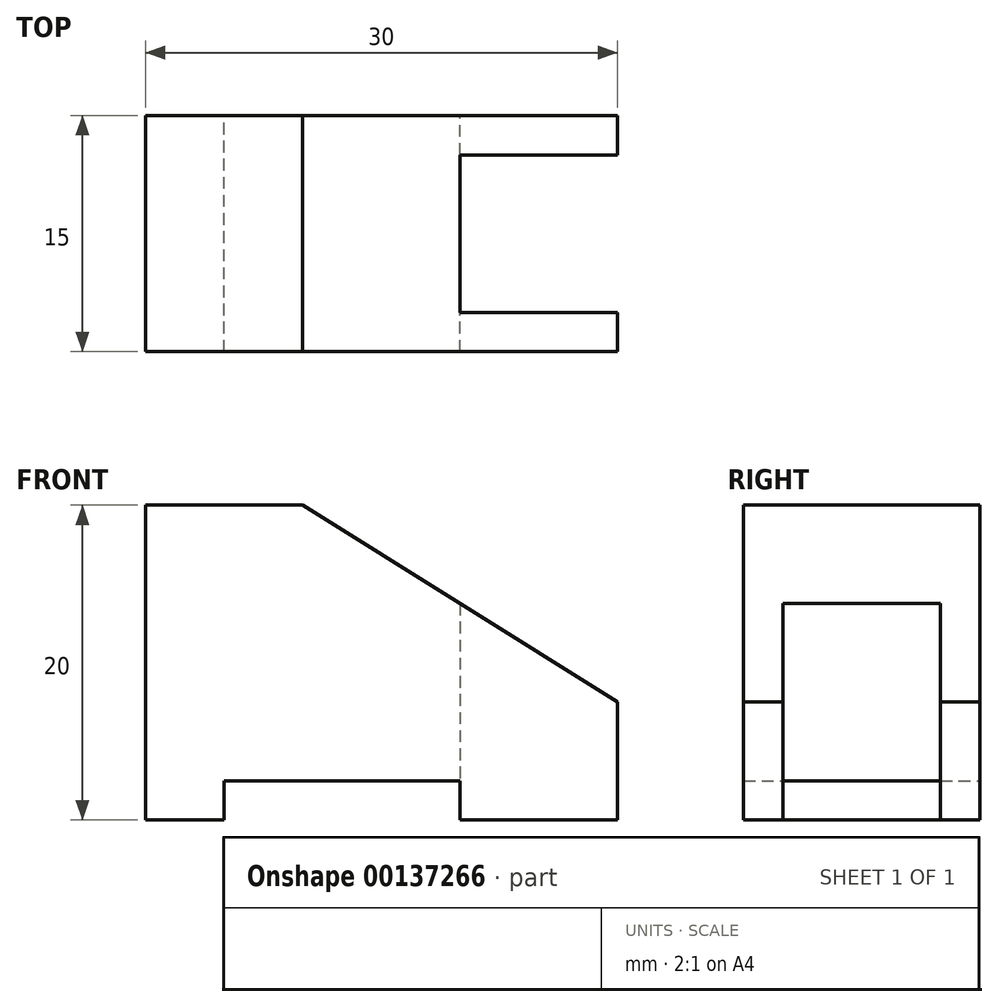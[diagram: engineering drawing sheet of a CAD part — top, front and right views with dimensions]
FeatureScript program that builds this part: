
annotation { "Feature Type Name" : "Feature", "Feature Type Description" : "" }
export const myFeature = defineFeature(function(context is Context, id is Id, definition is map)
    precondition{}
    {
        {
            var Q0;
            Q0=qCreatedBy(makeId("Front.planeOp"),FACE);
            var sketch = newSketch(context, id + "F0", { "sketchPlane" : qUnion([Q0])});
            skLineSegment(sketch, "E0", {"start": v(0, 0) * mm, "end": v(0, 20) * mm});
            skLineSegment(sketch, "E1", {"start": v(0, 20) * mm, "end": v(10, 20) * mm});
            skLineSegment(sketch, "E2", {"start": v(10, 20) * mm, "end": v(30, 7.5) * mm});
            skLineSegment(sketch, "E3", {"start": v(30, 7.5) * mm, "end": v(30, 0) * mm});
            skLineSegment(sketch, "E4", {"start": v(30, 0) * mm, "end": v(20, 0) * mm});
            skLineSegment(sketch, "E5", {"start": v(20, 0) * mm, "end": v(20, 2.5) * mm});
            skLineSegment(sketch, "E6", {"start": v(20, 2.5) * mm, "end": v(5, 2.5) * mm});
            skLineSegment(sketch, "E7", {"start": v(5, 2.5) * mm, "end": v(5, 0) * mm});
            skLineSegment(sketch, "E8", {"start": v(5, 0) * mm, "end": v(0, 0) * mm});
            skSolve(sketch);
        }
        {
            var Q0;
            Q0=makeQuery(id+"F0.imprint","IMPRINT",FACE,{"disambiguationData":[TD([[makeQuery(id+"F0.imprint","IMPRINT",EDGE,{"derivedFrom":sQuery(id+"F0.wireOp",EDGE,"E0")}),-1.0]])]});
            extrude(context, id + "F1", {"entities" : qUnion([Q0]), "depth" : 15 * mm});
        }
        {
            var Q0;
            Q0=makeQuery(id+"F1.opExtrude","SWEPT_FACE",FACE,{"disambiguationData":[OSD([sQuery(id+"F0.wireOp",EDGE,"E4")])]});
            var sketch = newSketch(context, id + "F2", { "sketchPlane" : qUnion([Q0])});
            skLineSegment(sketch, "E9", {"start": v(30, 2.5) * mm, "end": v(30, 12.5) * mm});
            skLineSegment(sketch, "E10", {"start": v(30, 12.5) * mm, "end": v(20, 12.5) * mm});
            skLineSegment(sketch, "E11", {"start": v(20, 12.5) * mm, "end": v(20, 2.5) * mm});
            skLineSegment(sketch, "E12", {"start": v(20, 2.5) * mm, "end": v(30, 2.5) * mm});
            skLineSegment(sketch, "E13.0", {"start": v(30, 15) * mm, "end": v(20, 15) * mm});
            skLineSegment(sketch, "E13.1", {"start": v(30, 0) * mm, "end": v(20, 0) * mm});
            skSolve(sketch);
        }
        {
            var Q0;
            Q0=makeQuery(id+"F2.imprint","IMPRINT",FACE,{"disambiguationData":[TD([[makeQuery(id+"F2.imprint","IMPRINT",EDGE,{"derivedFrom":sQuery(id+"F2.wireOp",EDGE,"E9")}),-1.0]])]});
            extrude(context, id + "F3", {"entities" : qUnion([Q0]), "operationType" : NewBodyOperationType.REMOVE, "oppositeDirection" : true, "depth" : 25 * mm});
        }
    });
